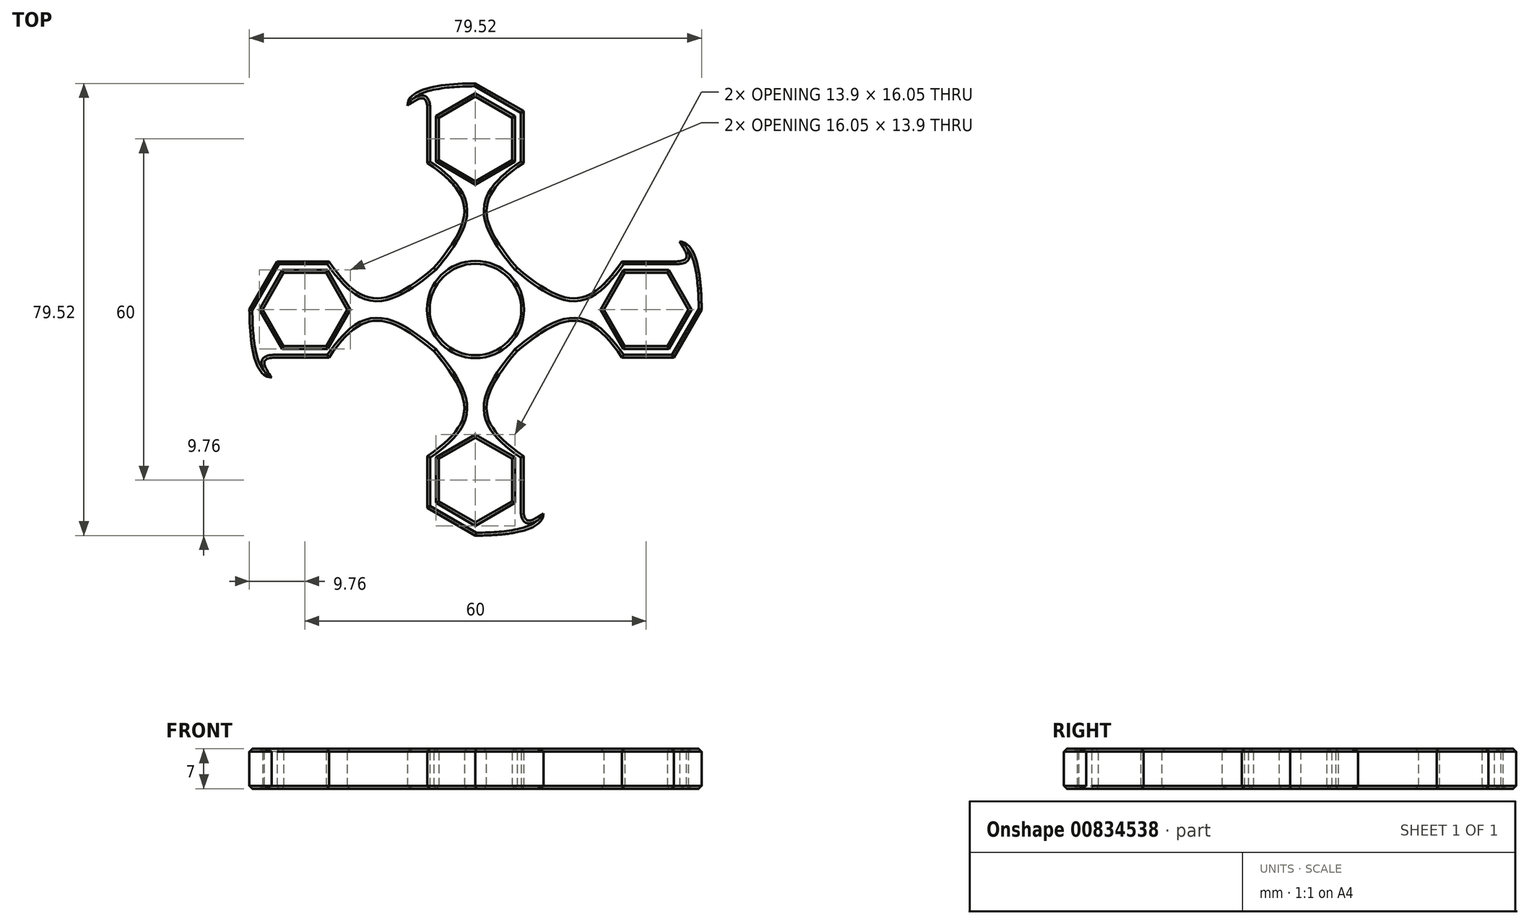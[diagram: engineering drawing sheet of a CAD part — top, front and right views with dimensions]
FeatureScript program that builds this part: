
annotation { "Feature Type Name" : "Feature", "Feature Type Description" : "" }
export const myFeature = defineFeature(function(context is Context, id is Id, definition is map)
    precondition{}
    {
        {
            var Q0;
            Q0=qCreatedBy(makeId("Top.planeOp"),FACE);
            var sketch = newSketch(context, id + "F0", { "sketchPlane" : qUnion([Q0])});
            skCircle(sketch, "E0", {"center": v(0, 0) * mm, "radius": 8.05 * mm});
            skCircle(sketch, "E1.cCircle", {"center": v(30, 0) * mm, "radius": 6.45 * mm, "construction": true});
            skLineSegment(sketch, "E1.0", {"start": v(33.72, 6.45) * mm, "end": v(37.45, 0) * mm});
            skLineSegment(sketch, "E1.1", {"start": v(37.45, 0) * mm, "end": v(33.72, -6.45) * mm});
            skLineSegment(sketch, "E1.2", {"start": v(33.72, -6.45) * mm, "end": v(26.28, -6.45) * mm});
            skLineSegment(sketch, "E1.3", {"start": v(26.28, -6.45) * mm, "end": v(22.55, 0) * mm});
            skLineSegment(sketch, "E1.4", {"start": v(22.55, 0) * mm, "end": v(26.28, 6.45) * mm});
            skLineSegment(sketch, "E1.5", {"start": v(26.28, 6.45) * mm, "end": v(33.72, 6.45) * mm});
            skLineSegment(sketch, "E2.1.0", {"start": v(6.45, 26.28) * mm, "end": v(0, 22.55) * mm});
            skLineSegment(sketch, "E2.1.1", {"start": v(-6.45, 26.28) * mm, "end": v(-6.45, 33.72) * mm});
            skLineSegment(sketch, "E2.1.2", {"start": v(0, 37.45) * mm, "end": v(6.45, 33.72) * mm});
            skCircle(sketch, "E2.1.3", {"center": v(0, 30) * mm, "radius": 6.45 * mm, "construction": true});
            skLineSegment(sketch, "E2.1.4", {"start": v(0, 22.55) * mm, "end": v(-6.45, 26.28) * mm});
            skPoint(sketch, "E2.1.5", {"position": v(-3.23, 35.59) * mm});
            skLineSegment(sketch, "E2.1.6", {"start": v(-6.45, 33.72) * mm, "end": v(0, 37.45) * mm});
            skLineSegment(sketch, "E2.1.7", {"start": v(6.45, 33.72) * mm, "end": v(6.45, 26.28) * mm});
            skLineSegment(sketch, "E2.2.0", {"start": v(-26.28, 6.45) * mm, "end": v(-22.55, 0) * mm});
            skLineSegment(sketch, "E2.2.1", {"start": v(-26.28, -6.45) * mm, "end": v(-33.72, -6.45) * mm});
            skLineSegment(sketch, "E2.2.2", {"start": v(-37.45, 0) * mm, "end": v(-33.72, 6.45) * mm});
            skCircle(sketch, "E2.2.3", {"center": v(-30, 0) * mm, "radius": 6.45 * mm, "construction": true});
            skLineSegment(sketch, "E2.2.4", {"start": v(-22.55, 0) * mm, "end": v(-26.28, -6.45) * mm});
            skPoint(sketch, "E2.2.5", {"position": v(-35.59, -3.23) * mm});
            skLineSegment(sketch, "E2.2.6", {"start": v(-33.72, -6.45) * mm, "end": v(-37.45, 0) * mm});
            skLineSegment(sketch, "E2.2.7", {"start": v(-33.72, 6.45) * mm, "end": v(-26.28, 6.45) * mm});
            skLineSegment(sketch, "E2.3.0", {"start": v(-6.45, -26.28) * mm, "end": v(0, -22.55) * mm});
            skLineSegment(sketch, "E2.3.1", {"start": v(6.45, -26.28) * mm, "end": v(6.45, -33.72) * mm});
            skLineSegment(sketch, "E2.3.2", {"start": v(0, -37.45) * mm, "end": v(-6.45, -33.72) * mm});
            skCircle(sketch, "E2.3.3", {"center": v(0, -30) * mm, "radius": 6.45 * mm, "construction": true});
            skLineSegment(sketch, "E2.3.4", {"start": v(0, -22.55) * mm, "end": v(6.45, -26.28) * mm});
            skPoint(sketch, "E2.3.5", {"position": v(3.22, -35.59) * mm});
            skLineSegment(sketch, "E2.3.6", {"start": v(6.45, -33.72) * mm, "end": v(0, -37.45) * mm});
            skLineSegment(sketch, "E2.3.7", {"start": v(-6.45, -33.72) * mm, "end": v(-6.45, -26.28) * mm});
            skSolve(sketch);
        }
        {
            var Q0;
            Q0=qCreatedBy(makeId("Top.planeOp"),FACE);
            var sketch = newSketch(context, id + "F1", { "sketchPlane" : qUnion([Q0])});
            skCircle(sketch, "E3.cCircle", {"center": v(0, 0) * mm, "radius": 10 * mm, "construction": true});
            skLineSegment(sketch, "E3.0", {"start": v(10, 2.68) * mm, "end": v(10, -2.68) * mm});
            skLineSegment(sketch, "E3.1", {"start": v(10, -2.68) * mm, "end": v(7.32, -7.32) * mm});
            skLineSegment(sketch, "E3.2", {"start": v(7.32, -7.32) * mm, "end": v(2.68, -10) * mm});
            skLineSegment(sketch, "E3.3", {"start": v(2.68, -10) * mm, "end": v(-2.68, -10) * mm});
            skLineSegment(sketch, "E3.4", {"start": v(-2.68, -10) * mm, "end": v(-7.32, -7.32) * mm});
            skLineSegment(sketch, "E3.5", {"start": v(-7.32, -7.32) * mm, "end": v(-10, -2.68) * mm});
            skLineSegment(sketch, "E3.6", {"start": v(-10, -2.68) * mm, "end": v(-10, 2.68) * mm});
            skLineSegment(sketch, "E3.7", {"start": v(-10, 2.68) * mm, "end": v(-7.32, 7.32) * mm});
            skLineSegment(sketch, "E3.8", {"start": v(-7.32, 7.32) * mm, "end": v(-2.68, 10) * mm});
            skLineSegment(sketch, "E3.9", {"start": v(-2.68, 10) * mm, "end": v(2.68, 10) * mm});
            skLineSegment(sketch, "E3.10", {"start": v(2.68, 10) * mm, "end": v(7.32, 7.32) * mm});
            skLineSegment(sketch, "E3.11", {"start": v(7.32, 7.32) * mm, "end": v(10, 2.68) * mm});
            skPoint(sketch, "E3.0.midPoint", {"position": v(10, 0) * mm});
            skPoint(sketch, "E4.0", {"position": v(30, 0) * mm});
            skLineSegment(sketch, "E5.0.0", {"start": v(33.72, 6.45) * mm, "end": v(26.28, 6.45) * mm});
            skLineSegment(sketch, "E5.0.1", {"start": v(26.28, 6.45) * mm, "end": v(22.55, 0) * mm});
            skLineSegment(sketch, "E5.0.2", {"start": v(22.55, 0) * mm, "end": v(26.28, -6.45) * mm});
            skLineSegment(sketch, "E5.0.3", {"start": v(26.28, -6.45) * mm, "end": v(33.72, -6.45) * mm});
            skLineSegment(sketch, "E5.0.4", {"start": v(33.72, -6.45) * mm, "end": v(37.45, 0) * mm});
            skLineSegment(sketch, "E5.0.5", {"start": v(37.45, 0) * mm, "end": v(33.72, 6.45) * mm});
            skLineSegment(sketch, "E6", {"start": v(33.72, 6.45) * mm, "end": v(26.28, -6.45) * mm, "construction": true});
            skFitSpline(sketch, "E7", {"points": [v(7.32, 7.32) * mm, v(25.78, 8.45) * mm], "startDerivative": vector(26.04, -21.96) * mm, "endDerivative": vector(17.33, 25.35) * mm});
            skLineSegment(sketch, "E8.0", {"start": v(34.88, 8.45) * mm, "end": v(25.78, 8.45) * mm});
            skLineSegment(sketch, "E8.1", {"start": v(39.76, 0) * mm, "end": v(34.88, 8.45) * mm});
            skLineSegment(sketch, "E8.2", {"start": v(34.88, -8.45) * mm, "end": v(39.76, 0) * mm});
            skLineSegment(sketch, "E8.3", {"start": v(25.78, -8.45) * mm, "end": v(34.88, -8.45) * mm});
            skFitSpline(sketch, "E9", {"points": [v(34.88, 8.45) * mm, v(35.88, 11.95) * mm], "startDerivative": vector(9, 0) * mm, "endDerivative": vector(-4.97, 7.5) * mm});
            skFitSpline(sketch, "E10", {"points": [v(35.88, 11.95) * mm, v(39.76, 0) * mm], "startDerivative": vector(9, 0) * mm, "endDerivative": vector(0, -18) * mm});
            skFitSpline(sketch, "E11.MirrorCS", {"points": [v(7.32, -7.32) * mm, v(25.78, -8.45) * mm], "startDerivative": vector(26.04, 21.96) * mm, "endDerivative": vector(17.33, -25.35) * mm});
            skCircle(sketch, "E12", {"center": v(35.88, 11.95) * mm, "radius": 3 * mm, "construction": true});
            skLineSegment(sketch, "E13.MirrorCS", {"start": v(-34.88, 8.45) * mm, "end": v(-25.78, 8.45) * mm});
            skLineSegment(sketch, "E14.MirrorCS", {"start": v(-39.76, 0) * mm, "end": v(-34.88, 8.45) * mm});
            skLineSegment(sketch, "E15.MirrorCS", {"start": v(-25.78, -8.45) * mm, "end": v(-34.88, -8.45) * mm});
            skLineSegment(sketch, "E16.MirrorCS", {"start": v(-34.88, -8.45) * mm, "end": v(-39.76, 0) * mm});
            skLineSegment(sketch, "E17.MirrorCS", {"start": v(-37.45, 0) * mm, "end": v(-33.72, 6.45) * mm});
            skLineSegment(sketch, "E18.MirrorCS", {"start": v(-33.72, -6.45) * mm, "end": v(-37.45, 0) * mm});
            skLineSegment(sketch, "E19.MirrorCS", {"start": v(-26.28, -6.45) * mm, "end": v(-33.72, -6.45) * mm});
            skLineSegment(sketch, "E20.MirrorCS", {"start": v(-22.55, 0) * mm, "end": v(-26.28, -6.45) * mm});
            skLineSegment(sketch, "E21.MirrorCS", {"start": v(-26.28, 6.45) * mm, "end": v(-22.55, 0) * mm});
            skLineSegment(sketch, "E22.MirrorCS", {"start": v(-33.72, 6.45) * mm, "end": v(-26.28, 6.45) * mm});
            skFitSpline(sketch, "E23", {"points": [v(-25.78, 8.45) * mm, v(-7.32, 7.32) * mm], "startDerivative": vector(17.33, -25.35) * mm, "endDerivative": vector(26.04, 21.96) * mm});
            skFitSpline(sketch, "E24", {"points": [v(-25.78, -8.45) * mm, v(-7.32, -7.32) * mm], "startDerivative": vector(17.33, 25.35) * mm, "endDerivative": vector(26.04, -21.96) * mm});
            skFitSpline(sketch, "E25.MirrorCS", {"points": [v(-34.88, -8.45) * mm, v(-35.88, -11.95) * mm], "startDerivative": vector(-9, 0) * mm, "endDerivative": vector(4.97, -7.5) * mm});
            skFitSpline(sketch, "E26.MirrorCS", {"points": [v(-35.88, -11.95) * mm, v(-39.76, 0) * mm], "startDerivative": vector(-9, 0) * mm, "endDerivative": vector(0, 18) * mm});
            skLineSegment(sketch, "E27.0", {"start": v(8.45, 34.88) * mm, "end": v(8.45, 25.78) * mm});
            skLineSegment(sketch, "E27.1", {"start": v(0, 39.76) * mm, "end": v(8.45, 34.88) * mm});
            skLineSegment(sketch, "E27.2", {"start": v(-8.45, 34.88) * mm, "end": v(0, 39.76) * mm});
            skFitSpline(sketch, "E28", {"points": [v(8.45, 25.78) * mm, v(7.32, 7.32) * mm], "startDerivative": vector(-25.35, -17.33) * mm, "endDerivative": vector(21.96, -26.04) * mm});
            skFitSpline(sketch, "E29.MirrorCS", {"points": [v(-8.45, 25.78) * mm, v(-7.32, 7.32) * mm], "startDerivative": vector(25.35, -17.33) * mm, "endDerivative": vector(-21.96, -26.04) * mm});
            skLineSegment(sketch, "E30", {"start": v(-8.45, 34.88) * mm, "end": v(-8.45, 25.78) * mm});
            skLineSegment(sketch, "E31.MirrorCS", {"start": v(-8.45, -34.88) * mm, "end": v(-8.45, -25.78) * mm});
            skLineSegment(sketch, "E32.MirrorCS", {"start": v(-8.45, -34.88) * mm, "end": v(0, -39.76) * mm});
            skLineSegment(sketch, "E33.MirrorCS", {"start": v(8.45, -34.88) * mm, "end": v(8.45, -25.78) * mm});
            skLineSegment(sketch, "E34.MirrorCS", {"start": v(0, -39.76) * mm, "end": v(8.45, -34.88) * mm});
            skFitSpline(sketch, "E35", {"points": [v(-7.32, -7.32) * mm, v(-8.45, -25.78) * mm], "startDerivative": vector(21.96, -26.04) * mm, "endDerivative": vector(-25.35, -17.33) * mm});
            skFitSpline(sketch, "E36", {"points": [v(7.32, -7.32) * mm, v(8.45, -25.78) * mm], "startDerivative": vector(-21.96, -26.04) * mm, "endDerivative": vector(25.35, -17.33) * mm});
            skFitSpline(sketch, "E37", {"points": [v(-8.45, 34.88) * mm, v(-11.95, 35.88) * mm], "startDerivative": vector(0, 9) * mm, "endDerivative": vector(-7.5, -4.97) * mm});
            skFitSpline(sketch, "E38", {"points": [v(-11.95, 35.88) * mm, v(0, 39.76) * mm], "startDerivative": vector(0, 9) * mm, "endDerivative": vector(18, 0) * mm});
            skCircle(sketch, "E39", {"center": v(-11.95, 35.88) * mm, "radius": 3 * mm, "construction": true});
            skFitSpline(sketch, "E40.MirrorCS", {"points": [v(8.45, -34.88) * mm, v(11.95, -35.88) * mm], "startDerivative": vector(0, -9) * mm, "endDerivative": vector(7.5, 4.97) * mm});
            skFitSpline(sketch, "E41.MirrorCS", {"points": [v(11.95, -35.88) * mm, v(0, -39.76) * mm], "startDerivative": vector(0, -9) * mm, "endDerivative": vector(-18, 0) * mm});
            skSolve(sketch);
        }
        {
            var Q0;
            Q0=makeQuery(id+"F1.imprint","IMPRINT",FACE,{"disambiguationData":[TD([[makeQuery(id+"F1.imprint","IMPRINT",EDGE,{"derivedFrom":sQuery(id+"F1.wireOp",EDGE,"E3.5")}),1.0]])]});
            var Q1;
            Q1=makeQuery(id+"F1.imprint","IMPRINT",FACE,{"disambiguationData":[TD([[makeQuery(id+"F1.imprint","IMPRINT",EDGE,{"derivedFrom":sQuery(id+"F1.wireOp",EDGE,"E3.8")}),1.0]])]});
            var Q2;
            Q2=makeQuery(id+"F1.imprint","IMPRINT",FACE,{"disambiguationData":[TD([[makeQuery(id+"F1.imprint","IMPRINT",EDGE,{"derivedFrom":sQuery(id+"F1.wireOp",EDGE,"E3.0")}),1.0]])]});
            var Q3;
            Q3=makeQuery(id+"F1.imprint","IMPRINT",FACE,{"disambiguationData":[TD([[makeQuery(id+"F1.imprint","IMPRINT",EDGE,{"derivedFrom":sQuery(id+"F1.wireOp",EDGE,"E3.2")}),1.0]])]});
            var Q4;
            Q4=makeQuery(id+"F1.imprint","IMPRINT",FACE,{"disambiguationData":[TD([[makeQuery(id+"F1.imprint","IMPRINT",EDGE,{"derivedFrom":sQuery(id+"F1.wireOp",EDGE,"E8.1")}),-1.0]])]});
            var Q5;
            Q5=makeQuery(id+"F1.imprint","IMPRINT",FACE,{"disambiguationData":[TD([[makeQuery(id+"F1.imprint","IMPRINT",EDGE,{"derivedFrom":sQuery(id+"F1.wireOp",EDGE,"E16.MirrorCS")}),1.0]])]});
            var Q6;
            Q6=makeQuery(id+"F1.imprint","IMPRINT",FACE,{"disambiguationData":[TD([[makeQuery(id+"F1.imprint","IMPRINT",EDGE,{"derivedFrom":sQuery(id+"F1.wireOp",EDGE,"E3.0")}),-1.0]])]});
            var Q7;
            Q7=makeQuery(id+"F1.imprint","IMPRINT",FACE,{"disambiguationData":[TD([[makeQuery(id+"F1.imprint","IMPRINT",EDGE,{"derivedFrom":sQuery(id+"F1.wireOp",EDGE,"E34.MirrorCS")}),-1.0]])]});
            var Q8;
            Q8=makeQuery(id+"F1.imprint","IMPRINT",FACE,{"disambiguationData":[TD([[makeQuery(id+"F1.imprint","IMPRINT",EDGE,{"derivedFrom":sQuery(id+"F1.wireOp",EDGE,"E27.2")}),1.0]])]});
            extrude(context, id + "F2", {"entities" : qUnion([Q0, Q1, Q2, Q3, Q4, Q5, Q6, Q7, Q8]), "depth" : 7 * mm, "offsetDistance" : 25 * mm});
        }
        {
            var Q0;
            Q0=makeQuery(id+"F0.imprint","IMPRINT",FACE,{"disambiguationData":[TD([[makeQuery(id+"F0.imprint","IMPRINT",EDGE,{"derivedFrom":sQuery(id+"F0.wireOp",EDGE,"E0")}),1.0]])]});
            var Q1;
            Q1=makeQuery(id+"F0.imprint","IMPRINT",FACE,{"disambiguationData":[TD([[makeQuery(id+"F0.imprint","IMPRINT",EDGE,{"derivedFrom":sQuery(id+"F0.wireOp",EDGE,"E2.3.0")}),-1.0]])]});
            var Q2;
            Q2=makeQuery(id+"F0.imprint","IMPRINT",FACE,{"disambiguationData":[TD([[makeQuery(id+"F0.imprint","IMPRINT",EDGE,{"derivedFrom":sQuery(id+"F0.wireOp",EDGE,"E2.1.0")}),-1.0]])]});
            extrude(context, id + "F3", {"entities" : qUnion([Q0, Q1, Q2]), "operationType" : NewBodyOperationType.REMOVE, "endBound" : BoundingType.THROUGH_ALL, "depth" : 25 * mm, "offsetDistance" : 25 * mm});
        }
        {
            var Q0;
            Q0=makeQuery(id+"F2.opExtrude","CAP_FACE",FACE,{"disambiguationData":[OSD([sQuery(id+"F1.wireOp",EDGE,"E5.0.0"),sQuery(id+"F1.wireOp",EDGE,"E5.0.1"),sQuery(id+"F1.wireOp",EDGE,"E5.0.2"),sQuery(id+"F1.wireOp",EDGE,"E5.0.3"),sQuery(id+"F1.wireOp",EDGE,"E5.0.4"),sQuery(id+"F1.wireOp",EDGE,"E5.0.5"),sQuery(id+"F1.wireOp",EDGE,"E7"),sQuery(id+"F1.wireOp",EDGE,"E8.0"),sQuery(id+"F1.wireOp",EDGE,"E8.2"),sQuery(id+"F1.wireOp",EDGE,"E8.3"),sQuery(id+"F1.wireOp",EDGE,"E9"),sQuery(id+"F1.wireOp",EDGE,"E10"),sQuery(id+"F1.wireOp",EDGE,"E11.MirrorCS"),sQuery(id+"F1.wireOp",EDGE,"E13.MirrorCS"),sQuery(id+"F1.wireOp",EDGE,"E14.MirrorCS"),sQuery(id+"F1.wireOp",EDGE,"E15.MirrorCS"),sQuery(id+"F1.wireOp",EDGE,"E17.MirrorCS"),sQuery(id+"F1.wireOp",EDGE,"E18.MirrorCS"),sQuery(id+"F1.wireOp",EDGE,"E19.MirrorCS"),sQuery(id+"F1.wireOp",EDGE,"E20.MirrorCS"),sQuery(id+"F1.wireOp",EDGE,"E21.MirrorCS"),sQuery(id+"F1.wireOp",EDGE,"E22.MirrorCS"),sQuery(id+"F1.wireOp",EDGE,"E23"),sQuery(id+"F1.wireOp",EDGE,"E24"),sQuery(id+"F1.wireOp",EDGE,"E25.MirrorCS"),sQuery(id+"F1.wireOp",EDGE,"E26.MirrorCS"),sQuery(id+"F1.wireOp",EDGE,"E27.0"),sQuery(id+"F1.wireOp",EDGE,"E27.1"),sQuery(id+"F1.wireOp",EDGE,"E28"),sQuery(id+"F1.wireOp",EDGE,"E29.MirrorCS"),sQuery(id+"F1.wireOp",EDGE,"E30"),sQuery(id+"F1.wireOp",EDGE,"E31.MirrorCS"),sQuery(id+"F1.wireOp",EDGE,"E32.MirrorCS"),sQuery(id+"F1.wireOp",EDGE,"E33.MirrorCS"),sQuery(id+"F1.wireOp",EDGE,"E35"),sQuery(id+"F1.wireOp",EDGE,"E36"),sQuery(id+"F1.wireOp",EDGE,"E37"),sQuery(id+"F1.wireOp",EDGE,"E38"),sQuery(id+"F1.wireOp",EDGE,"E40.MirrorCS"),sQuery(id+"F1.wireOp",EDGE,"E41.MirrorCS")])],"isStart":false});
            var Q1;
            Q1=makeQuery(id+"F2.opExtrude","CAP_FACE",FACE,{"disambiguationData":[OSD([sQuery(id+"F1.wireOp",EDGE,"E5.0.0"),sQuery(id+"F1.wireOp",EDGE,"E5.0.1"),sQuery(id+"F1.wireOp",EDGE,"E5.0.2"),sQuery(id+"F1.wireOp",EDGE,"E5.0.3"),sQuery(id+"F1.wireOp",EDGE,"E5.0.4"),sQuery(id+"F1.wireOp",EDGE,"E5.0.5"),sQuery(id+"F1.wireOp",EDGE,"E7"),sQuery(id+"F1.wireOp",EDGE,"E8.0"),sQuery(id+"F1.wireOp",EDGE,"E8.2"),sQuery(id+"F1.wireOp",EDGE,"E8.3"),sQuery(id+"F1.wireOp",EDGE,"E9"),sQuery(id+"F1.wireOp",EDGE,"E10"),sQuery(id+"F1.wireOp",EDGE,"E11.MirrorCS"),sQuery(id+"F1.wireOp",EDGE,"E13.MirrorCS"),sQuery(id+"F1.wireOp",EDGE,"E14.MirrorCS"),sQuery(id+"F1.wireOp",EDGE,"E15.MirrorCS"),sQuery(id+"F1.wireOp",EDGE,"E17.MirrorCS"),sQuery(id+"F1.wireOp",EDGE,"E18.MirrorCS"),sQuery(id+"F1.wireOp",EDGE,"E19.MirrorCS"),sQuery(id+"F1.wireOp",EDGE,"E20.MirrorCS"),sQuery(id+"F1.wireOp",EDGE,"E21.MirrorCS"),sQuery(id+"F1.wireOp",EDGE,"E22.MirrorCS"),sQuery(id+"F1.wireOp",EDGE,"E23"),sQuery(id+"F1.wireOp",EDGE,"E24"),sQuery(id+"F1.wireOp",EDGE,"E25.MirrorCS"),sQuery(id+"F1.wireOp",EDGE,"E26.MirrorCS"),sQuery(id+"F1.wireOp",EDGE,"E27.0"),sQuery(id+"F1.wireOp",EDGE,"E27.1"),sQuery(id+"F1.wireOp",EDGE,"E28"),sQuery(id+"F1.wireOp",EDGE,"E29.MirrorCS"),sQuery(id+"F1.wireOp",EDGE,"E30"),sQuery(id+"F1.wireOp",EDGE,"E31.MirrorCS"),sQuery(id+"F1.wireOp",EDGE,"E32.MirrorCS"),sQuery(id+"F1.wireOp",EDGE,"E33.MirrorCS"),sQuery(id+"F1.wireOp",EDGE,"E35"),sQuery(id+"F1.wireOp",EDGE,"E36"),sQuery(id+"F1.wireOp",EDGE,"E37"),sQuery(id+"F1.wireOp",EDGE,"E38"),sQuery(id+"F1.wireOp",EDGE,"E40.MirrorCS"),sQuery(id+"F1.wireOp",EDGE,"E41.MirrorCS")])],"isStart":true});
            chamfer(context, id + "F4", {"entities" : qUnion([Q0, Q1]), "width" : 0.5 * mm, "tangentPropagation" : true});
        }
    });
